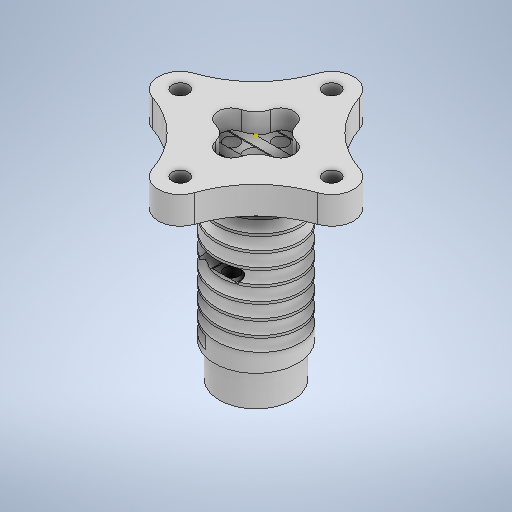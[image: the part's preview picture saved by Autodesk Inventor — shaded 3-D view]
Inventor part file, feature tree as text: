
AUTODESK INVENTOR PART (.ipt)
format: ipt  version: 2025.2 (Build 292293000, 293)  size: 1,427,456 bytes
history: native  units: mm
features: sketch x17, extrude x12, projected_geometry x3, plane x1, helix x1, chamfer x1, mirror x1, other x1
ambient origin geometry x8: Origin, YZ Plane, XZ Plane, XY Plane, X Axis, Y Axis, Z Axis, Center Point
bodies: Solid1 (feature_tree)
feature tree (37):
  extrude  "Extrusion1"  Depth=9.0mm
  extrude  "Extrusion2"  Depth=9.0mm
  extrude  "Extrusion3"  Depth=15.5mm
  plane  "Work Plane1"
  helix  "Coil2"  [1 undecoded]
  extrude  "Extrusion4"  Depth=20.0mm
  extrude  "Extrusion5"  Depth=20.0mm
  extrude  "Extrusion6"  Depth=5.0mm TaperAngle=0.0deg
  extrude  "Extrusion7"  Depth=38.0mm TaperAngle=0.0deg
  extrude  "Extrusion8"  Depth=7.0mm TaperAngle=0.0deg
  chamfer  "Chamfer1"  [1 undecoded]
  extrude  "Extrusion9"  Depth=4.5mm
  sketch  "Sketch13"  dims[d47=1.5mm]
  mirror  "Mirror1"
  extrude  "Extrusion10"  Depth=0.6mm
  extrude  "Extrusion11"  Depth=0.6mm TaperAngle=360.0deg
  extrude  "Extrusion12"  Depth=4.0mm
  sketch  "Sketch1"  dims[d0=9.0mm d1=9.0mm]
  sketch  "Sketch2"  dims[d5=31.0mm d6=31.0mm d10=15.5mm]
  sketch  "Sketch3"  dims[d13=20.0mm d14=20.0mm]
  other  "Work Axis2"
  sketch  "Sketch6"  dims[d18=17.0mm d19=38.0mm d20=0.0mm]
  sketch  "Sketch7"  dims[d21=15.0mm d22=7.0mm d23=0.0mm]
  sketch  "Sketch8"  dims[d33=135.0deg]
  sketch  "Sketch Circular Pattern1"  dims[d2=9.0mm d3=9.0mm]
  sketch  "Sketch9"  dims[d34=2.5mm]
  sketch  "Sketch Circular Pattern2"  dims[d11=15.5mm d12=20.0mm]
  sketch  "Sketch10"  dims[d35=3.0mm d36=27.25mm d37=80.0mm d38=0.0mm d39=90.0deg d40=90.0deg d41=0.0mm d42=0.0mm]
  sketch  "Sketch11"  dims[d45=5.0mm]
  sketch  "Sketch Circular Pattern3"  dims[d15=20.0mm d16=5.0mm d17=0.0mm]
  sketch  "Sketch12"  dims[d46=1.5mm]
  sketch  "Sketch14"  dims[d49=14.875mm]
  projected_geometry  "Projected Loop1"
  sketch  "Sketch15"  dims[d50=3.0mm]
  projected_geometry  "Projected Loop2"
  sketch  "Sketch16"  dims[d51=5.0mm d52=0.0mm d53=0.0mm d54=4.5mm d55=5.5mm d56=40.0mm d58=360.0deg d60=4.0mm d61=4.0mm d62=4.0mm d63=4.0mm d64=3.5mm d65=0.0mm d66=3.0mm d67=40.0mm d69=360.0deg d71=0.0mm d72=0.0mm d73=4.5mm d74=4.0mm d75=0.0mm d76=3.3mm d77=40.0mm d79=360.0deg d81=0.0mm d82=0.0mm d83=1.35mm d84=2.0mm d85=45.0deg d86=4.45mm d87=7.5mm d88=0.0mm d89=0.2mm d90=0.0mm d91=0.2mm d92=0.0mm d93=0.6mm d94=0.0mm]
  projected_geometry  "Projected Loop3"
note: 2 required parameter values undecoded (feature->parameter linkage not recoverable at this tier; creation-order binding heuristic only, values carry confidence <= 0.55)
